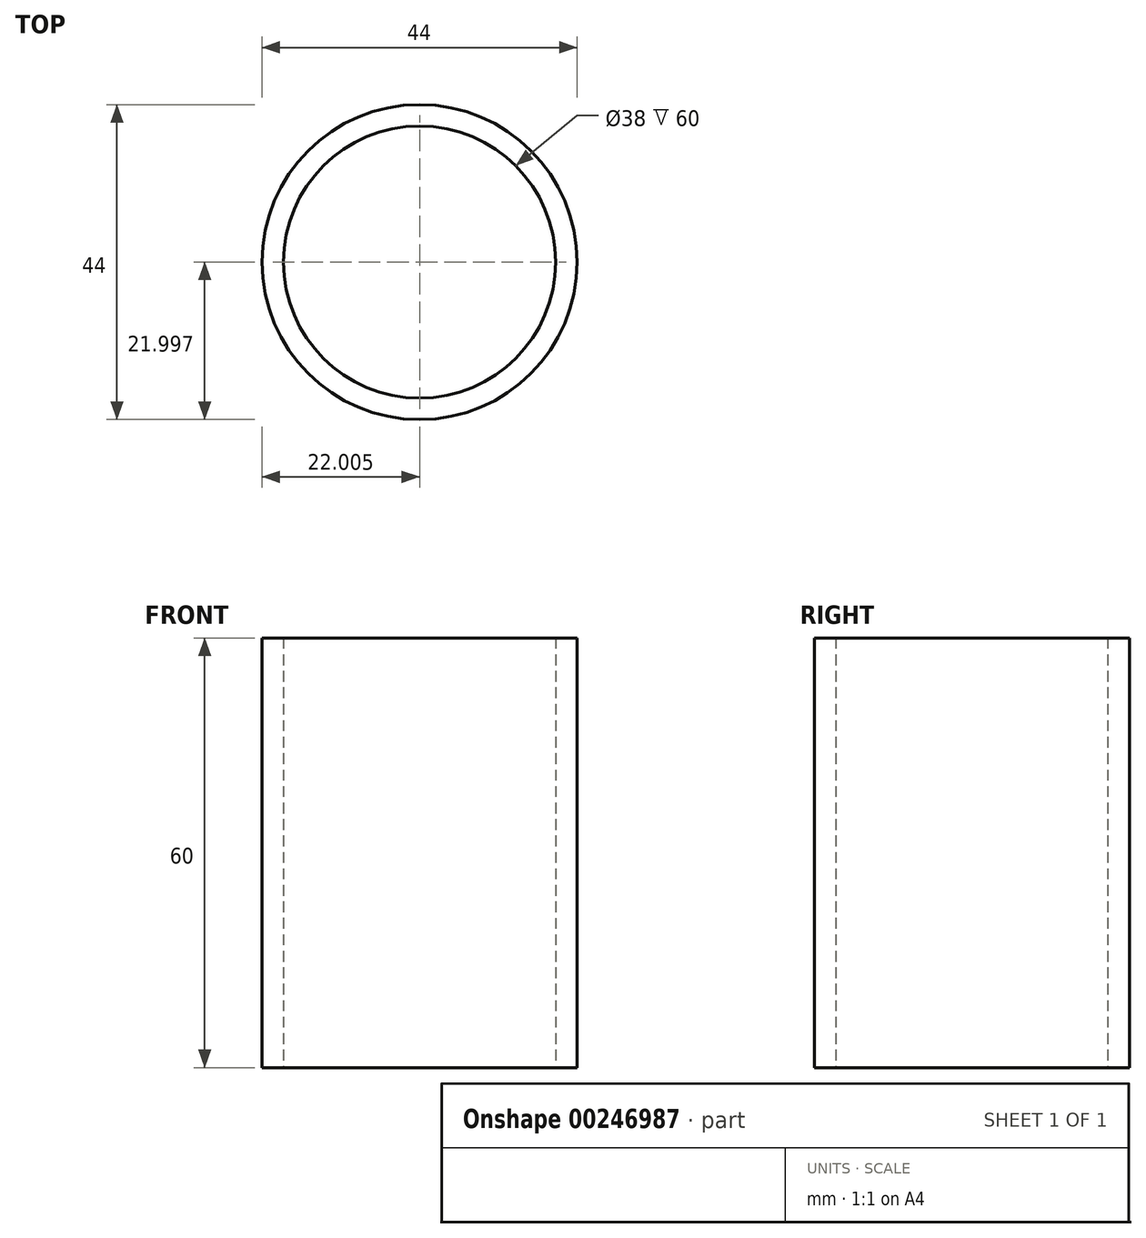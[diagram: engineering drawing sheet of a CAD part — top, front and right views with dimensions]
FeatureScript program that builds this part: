
annotation { "Feature Type Name" : "Feature", "Feature Type Description" : "" }
export const myFeature = defineFeature(function(context is Context, id is Id, definition is map)
    precondition{}
    {
        {
            var Q0;
            Q0=qCreatedBy(makeId("Top.planeOp"),FACE);
            var sketch = newSketch(context, id + "F0", { "sketchPlane" : qUnion([Q0])});
            skCircle(sketch, "E0", {"center": v(-91.09, 11.79) * mm, "radius": 19 * mm});
            skCircle(sketch, "E1", {"center": v(-91.09, 11.79) * mm, "radius": 22 * mm});
            skSolve(sketch);
        }
        {
            var Q0;
            Q0=makeQuery(id+"F0.imprint","IMPRINT",FACE,{"disambiguationData":[TD([[makeQuery(id+"F0.imprint","IMPRINT",EDGE,{"derivedFrom":sQuery(id+"F0.wireOp",EDGE,"E0")}),-1.0]])]});
            extrude(context, id + "F1", {"entities" : qUnion([Q0]), "depth" : 60 * mm});
        }
    });
